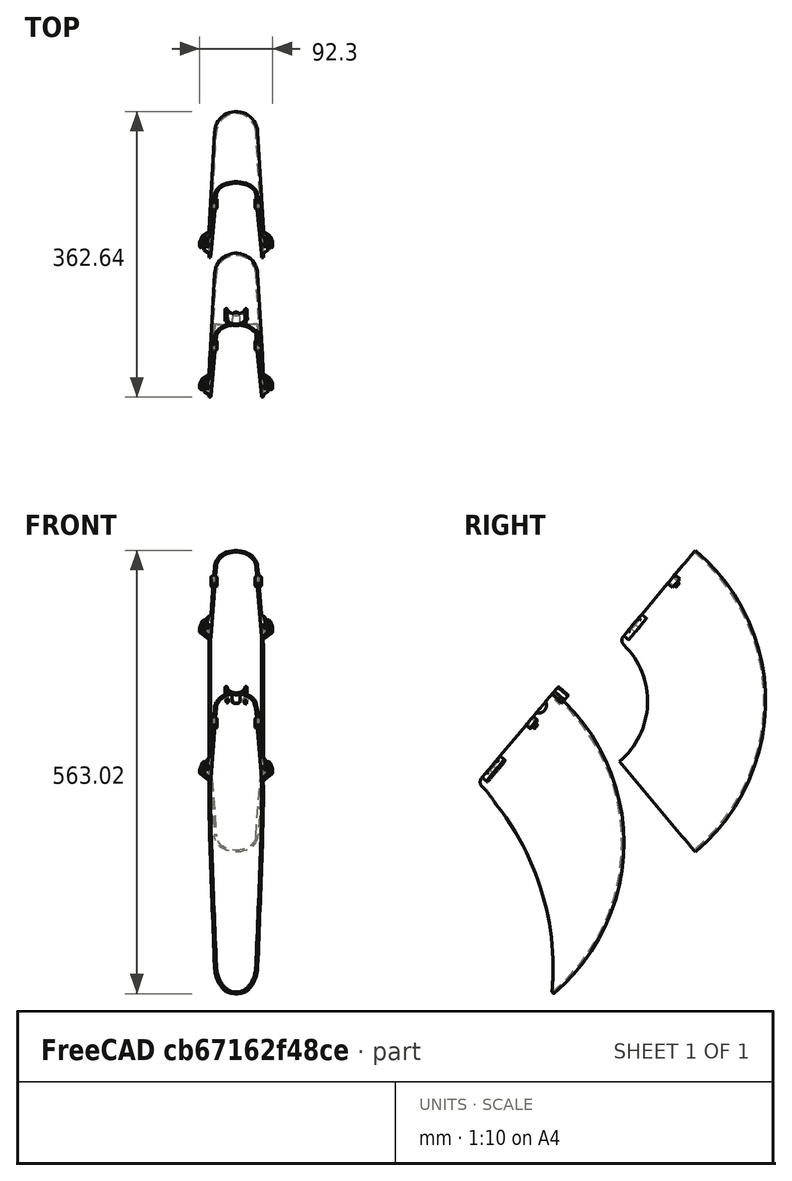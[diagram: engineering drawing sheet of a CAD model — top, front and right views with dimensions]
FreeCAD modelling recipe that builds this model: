
FCSTD DOCUMENT  (FreeCAD 0.19R)
Label: Mudguard5.1
License: All rights reserved
LicenseURL: http://en.wikipedia.org/wiki/All_rights_reserved
objects: Sketcher::SketchObject×6, Part::Cylinder×4, Part::Fillet×4, PartDesign::Fillet×3, PartDesign::Pocket×3, Part::Box×3, Part::MultiFuse×3, Part::Chamfer×3, Part::Cut×2, PartDesign::Revolution×1, PartDesign::ShapeBinder×1, PartDesign::Pad×1, PartDesign::Chamfer×1, PartDesign::Body×1, Mesh::Feature×1
note: 45 computed .brp shape members not serialized (recipe doc carries the construction recipe); baked Part::Feature solids carry a one-line shape summary decoded from their .brp

FEATURE [Sketcher::SketchObject] Sketch
  FullyConstrained = true
  MapMode = 5
  Support = -> [XY_Plane]
  sketch-geometry (9):
    g0: LineSegment StartX=-38.02 StartY=250 StartZ=0 EndX=36.46 EndY=250 EndZ=0
    g1: ArcOfCircle CenterX=1e-16 CenterY=222.456 CenterZ=0 NormalX=0 NormalY=0 NormalZ=1 AngleXU=0 Radius=27.5438 StartAngle=0.0563879 EndAngle=3.0852
    g2: ArcOfCircle CenterX=0 CenterY=222.257 CenterZ=0 NormalX=0 NormalY=0 NormalZ=1 AngleXU=0 Radius=25.0571 StartAngle=0.0604304 EndAngle=3.08116
    g3: LineSegment StartX=-34.5 StartY=100 StartZ=0 EndX=-27.5 EndY=224.009 EndZ=0
    g4: LineSegment StartX=-32.5 StartY=100 StartZ=0 EndX=-25.0114 EndY=223.77 EndZ=0
    g5: LineSegment StartX=25.0114 StartY=223.77 StartZ=0 EndX=32.5 EndY=100 EndZ=0
    g6: LineSegment StartX=-34.5 StartY=100 StartZ=0 EndX=-32.5 EndY=100 EndZ=0
    g7: LineSegment StartX=32.5 StartY=100 StartZ=0 EndX=34.5 EndY=100 EndZ=0
    g8: LineSegment StartX=34.5 StartY=100 StartZ=0 EndX=27.5 EndY=224.009 EndZ=0
  constraints (24):
    c: Horizontal(g0)
    c: DistanceY(g0) = 250
    c: Tangent(g1,g0)
    c: Symmetric(g1,g1,g-2)
    c: Distance(g0) = 74.48
    c: DistanceX(g0) = 36.46
    c: Tangent(g3,g1) = 1.5708
    c: Coincident(g6,g3)
    c: Coincident(g6,g4)
    c: Distance(g6) = 2
    c: Tangent(g4,g2) = 1.5708
    c: Tangent(g5,g2) = 1.5708
    c: PointOnObject(g2,g-2)
    c: Coincident(g5,g7)
    c: Coincident(g7,g8)
    c: Coincident(g8,g1)
    c: Symmetric(g5,g4,g-2)
    c: Symmetric(g7,g3,g-2)
    c: Horizontal(g7)
    c: Distance(g5,g4) = 65
    c: DistanceY(g7) = 100
    c: Distance(g1,g1) = 55
    c: Distance(g2,g1) = 2.5
    c: DistanceY(g2) = 223.77
FEATURE [PartDesign::Revolution] Revolution
  Angle = 100
  Axis = (1,0,0)
  Base = (0,0,0)
  Midplane = true
  Profile = -> Sketch
  ReferenceAxis = -> Sketch [H_Axis]
FEATURE [PartDesign::ShapeBinder] CopyFusion
  Placement = pos=(0,0,0) rot=(1,0,0;0.785398rad)
  TraceSupport = false
FEATURE [PartDesign::Fillet] Fillet
  Base = -> Revolution [Edge7,Edge19]
  BaseFeature = -> Revolution
  Radius = 8
  SupportTransform = false
FEATURE [Sketcher::SketchObject] Sketch002
  FullyConstrained = false
  MapMode = 5
  Placement = pos=(0,0,0) rot=(1,0,0;0.872665rad)
  Support = -> [Fillet]
  sketch-geometry (21):
    g0: LineSegment StartX=-29.785 StartY=256.106 StartZ=0 EndX=29.785 EndY=256.106 EndZ=0
    g1: LineSegment StartX=-43.3942 StartY=132.698 StartZ=0 EndX=-46.5 EndY=121.106 EndZ=0
    g2: LineSegment StartX=-46.5 StartY=121.106 StartZ=0 EndX=-33.2488 EndY=107.855 EndZ=0
    g3: LineSegment StartX=-33.2488 StartY=107.855 StartZ=0 EndX=-31 EndY=145.092 EndZ=0
    g4: LineSegment StartX=-31 StartY=145.092 StartZ=0 EndX=-43.3942 EndY=132.698 EndZ=0
    g5: LineSegment StartX=43.3942 StartY=132.698 StartZ=0 EndX=46.5 EndY=121.106 EndZ=0
    g6: LineSegment StartX=46.5 StartY=121.106 StartZ=0 EndX=33.2488 EndY=107.855 EndZ=0
    g7: LineSegment StartX=33.2488 StartY=107.855 StartZ=0 EndX=31 EndY=145.092 EndZ=0
    g8: LineSegment StartX=31 StartY=145.092 StartZ=0 EndX=43.3942 EndY=132.698 EndZ=0
    g9: LineSegment StartX=28 StartY=194.106 StartZ=0 EndX=32 EndY=198.106 EndZ=0
    g10: LineSegment StartX=32 StartY=198.106 StartZ=0 EndX=32 EndY=206.106 EndZ=0
    g11: LineSegment StartX=32 StartY=206.106 StartZ=0 EndX=28 EndY=210.106 EndZ=0
    g12: LineSegment StartX=28 StartY=210.106 StartZ=0 EndX=24 EndY=206.106 EndZ=0
    g13: LineSegment StartX=24 StartY=206.106 StartZ=0 EndX=24 EndY=198.106 EndZ=0
    g14: LineSegment StartX=24 StartY=198.106 StartZ=0 EndX=28 EndY=194.106 EndZ=0
    g15: LineSegment StartX=-28 StartY=194.106 StartZ=0 EndX=-24 EndY=198.106 EndZ=0
    g16: LineSegment StartX=-24 StartY=198.106 StartZ=0 EndX=-24 EndY=206.106 EndZ=0
    g17: LineSegment StartX=-24 StartY=206.106 StartZ=0 EndX=-28 EndY=210.106 EndZ=0
    g18: LineSegment StartX=-28 StartY=210.106 StartZ=0 EndX=-32 EndY=206.106 EndZ=0
    g19: LineSegment StartX=-32 StartY=206.106 StartZ=0 EndX=-32 EndY=198.106 EndZ=0
    g20: LineSegment StartX=-32 StartY=198.106 StartZ=0 EndX=-28 EndY=194.106 EndZ=0
  constraints (55):
    c: Coincident(g1,g2)
    c: Coincident(g2,g3)
    c: Coincident(g3,g4)
    c: Coincident(g4,g1)
    c: Coincident(g5,g6)
    c: Coincident(g6,g7)
    c: Coincident(g7,g8)
    c: Coincident(g8,g5)
    c: Symmetric(g7,g3,g-2)
    c: Symmetric(g6,g2,g-2)
    c: Equal(g5,g1)
    c: Symmetric(g5,g1,g-2)
    c: Equal(g2,g6)
    c: Distance(g5,g1) = 93
    c: Angle(g6) = -2.35619
    c: Coincident(g9,g10)
    c: Vertical(g10)
    c: Coincident(g10,g11)
    c: Coincident(g11,g12)
    c: Coincident(g12,g13)
    c: Vertical(g13)
    c: Coincident(g13,g14)
    c: Coincident(g14,g9)
    c: Coincident(g15,g16)
    c: Coincident(g16,g17)
    c: Coincident(g17,g18)
    c: Coincident(g18,g19)
    c: Coincident(g19,g20)
    c: Coincident(g20,g15)
    c: Distance(g5) = 12
    c: Angle(g5) = -1.309
    c: Symmetric(g0,g0,g-2)
    c: Distance(g0) = 59.57
    c: Angle(g8) = -0.785398
    c: Distance(g7,g3) = 62
    c: Distance(g9,g13) = 8
    c: Symmetric(g13,g15,g-2)
    c: Symmetric(g12,g16,g-2)
    c: Symmetric(g9,g19,g-2)
    c: Symmetric(g10,g18,g-2)
    c: Equal(g13,g19)
    c: Distance(g10) = 8
    c: Angle(g12,g11) = 1.5708
    c: Equal(g18,g12)
    c: Equal(g20,g14)
    c: Equal(g15,g9)
    c: Equal(g17,g11)
    c: Angle(g15,g20) = 1.5708
    c: Equal(g20,g15)
    c: Distance(g10,g0) = 50
    c: DistanceY(g12,g10) = 0
    c: Distance(g9,g19) = 64
    c: Distance(g5,g0) = 135
    c: Distance(g2) = 18.74
    c: Equal(g17,g18)
FEATURE [Sketcher::SketchObject] Sketch004
  FullyConstrained = false
  MapMode = 5
  Placement = pos=(-31,0,0) rot=(0.57735,-0.57735,-0.57735;2.0944rad)
  sketch-geometry (8):
    g0: LineSegment StartX=-122.627 StartY=164.31 StartZ=0 EndX=-119.228 EndY=159.366 EndZ=0
    g1: LineSegment StartX=-119.228 StartY=159.366 StartZ=0 EndX=-116.756 EndY=161.065 EndZ=0
    g2: LineSegment StartX=-116.756 StartY=161.065 StartZ=0 EndX=-120.154 EndY=166.009 EndZ=0
    g3: LineSegment StartX=-120.154 StartY=166.009 StartZ=0 EndX=-122.627 EndY=164.31 EndZ=0
    g4: LineSegment StartX=-76.9755 StartY=93.1865 StartZ=0 EndX=-79.4599 EndY=91.5049 EndZ=0
    g5: LineSegment StartX=-79.4599 StartY=91.5049 StartZ=0 EndX=-82.8231 EndY=96.4737 EndZ=0
    g6: LineSegment StartX=-82.8231 StartY=96.4737 StartZ=0 EndX=-80.3387 EndY=98.1553 EndZ=0
    g7: LineSegment StartX=-80.3387 StartY=98.1553 StartZ=0 EndX=-76.9755 EndY=93.1865 EndZ=0
  constraints (18):
    c: Coincident(g0,g1)
    c: Coincident(g1,g2)
    c: Coincident(g2,g3)
    c: Coincident(g3,g0)
    c: Coincident(g4,g5)
    c: Coincident(g5,g6)
    c: Coincident(g6,g7)
    c: Coincident(g7,g4)
    c: Equal(g1,g3)
    c: Equal(g3,g6)
    c: Equal(g6,g4)
    c: Distance(g6) = 3
    c: Perpendicular(g0,g3)
    c: Equal(g2,g0)
    c: Equal(g0,g5)
    c: Equal(g5,g7)
    c: Distance(g0) = 6
    c: Perpendicular(g5,g4)
FEATURE [Part::Cylinder] Cylinder001
  Angle = 360
  AttacherType = Attacher::AttachEngine3D
  Height = 250
  Placement = pos=(-100,-174,-159) rot=(0,1,0;1.5708rad)
  Radius = 334
FEATURE [Part::Cylinder] Cylinder
  Angle = 360
  AttacherType = Attacher::AttachEngine3D
  Height = 20
  Placement = pos=(35,142,175) rot=(0,-0.999201,0.039968;1.5708rad)
  Radius = 10
FEATURE [PartDesign::Pad] Pad
  BaseFeature = -> Fillet
  Direction = (1,1,1)
  Length = 8
  Length2 = 100
  Profile = -> Sketch002
  Reversed = true
  Type = 0
FEATURE [Sketcher::SketchObject] Sketch003
  FullyConstrained = true
  MapMode = 5
  Placement = pos=(0,-4.35e-14,3.65e-14) rot=(1,0,0;0.872665rad)
  Support = -> [Pad]
  sketch-geometry (8):
    g0: LineSegment StartX=35 StartY=146.87 StartZ=0 EndX=45 EndY=97.88 EndZ=0
    g1: LineSegment StartX=45 StartY=97.88 StartZ=0 EndX=47.9394 EndY=98.48 EndZ=0
    g2: LineSegment StartX=47.9394 StartY=98.48 StartZ=0 EndX=37.9394 EndY=147.47 EndZ=0
    g3: LineSegment StartX=37.9394 StartY=147.47 StartZ=0 EndX=35 EndY=146.87 EndZ=0
    g4: LineSegment StartX=-47.9394 StartY=98.48 StartZ=0 EndX=-45 EndY=97.88 EndZ=0
    g5: LineSegment StartX=-45 StartY=97.88 StartZ=0 EndX=-35 EndY=146.87 EndZ=0
    g6: LineSegment StartX=-47.9394 StartY=98.48 StartZ=0 EndX=-37.9394 EndY=147.47 EndZ=0
    g7: LineSegment StartX=-37.9394 StartY=147.47 StartZ=0 EndX=-35 EndY=146.87 EndZ=0
  constraints (22):
    c: Coincident(g0,g1)
    c: Coincident(g1,g2)
    c: Coincident(g2,g3)
    c: Coincident(g3,g0)
    c: Coincident(g4,g5)
    c: Equal(g1,g3)
    c: Equal(g0,g2)
    c: Symmetric(g4,g0,g-2)
    c: Perpendicular(g0,g1)
    c: Distance(g3) = 3
    c: Distance(g0,g4) = 90
    c: Coincident(g4,g6)
    c: Coincident(g6,g7)
    c: Coincident(g7,g5)
    c: Equal(g7,g3)
    c: Equal(g6,g5)
    c: Perpendicular(g6,g7)
    c: Symmetric(g0,g5,g-2)
    c: Distance(g2) = 50
    c: Equal(g4,g7)
    c: DistanceY(g0) = 97.88
    c: Distance(g5,g0) = 70
FEATURE [PartDesign::Pocket] Pocket
  BaseFeature = -> Pad
  Length = 2
  Length2 = 100
  Profile = -> Sketch003
  Type = 0
FEATURE [PartDesign::Chamfer] Chamfer
  Angle = 45
  Base = -> Pocket [Edge139,Edge101,Edge142,Edge145]
  BaseFeature = -> Pocket
  ChamferType = 0
  FlipDirection = false
  Size = 1
  Size2 = 1
  SupportTransform = false
FEATURE [Sketcher::SketchObject] Sketch005
  FullyConstrained = false
  MapMode = 5
  Placement = pos=(-3.5e-15,6.12836,-5.1423) rot=(0,0.906308,0.422618;3.14159rad)
  Support = -> [Chamfer]
  sketch-geometry (8):
    g0: LineSegment StartX=-37.5477 StartY=128.579 StartZ=0 EndX=-34.5477 EndY=128.579 EndZ=0
    g1: LineSegment StartX=-34.5477 StartY=128.579 StartZ=0 EndX=-34.5477 EndY=121.579 EndZ=0
    g2: LineSegment StartX=-34.5477 StartY=121.579 StartZ=0 EndX=-37.5477 EndY=121.579 EndZ=0
    g3: LineSegment StartX=-37.5477 StartY=121.579 StartZ=0 EndX=-37.5477 EndY=128.579 EndZ=0
    g4: LineSegment StartX=34.5477 StartY=128.579 StartZ=0 EndX=37.5477 EndY=128.579 EndZ=0
    g5: LineSegment StartX=37.5477 StartY=128.579 StartZ=0 EndX=37.5477 EndY=121.579 EndZ=0
    g6: LineSegment StartX=37.5477 StartY=121.579 StartZ=0 EndX=34.5477 EndY=121.579 EndZ=0
    g7: LineSegment StartX=34.5477 StartY=121.579 StartZ=0 EndX=34.5477 EndY=128.579 EndZ=0
  constraints (21):
    c: Coincident(g0,g1)
    c: Coincident(g1,g2)
    c: Coincident(g2,g3)
    c: Coincident(g3,g0)
    c: Horizontal(g0)
    c: Horizontal(g2)
    c: Vertical(g1)
    c: Vertical(g3)
    c: Coincident(g4,g5)
    c: Coincident(g5,g6)
    c: Coincident(g6,g7)
    c: Coincident(g7,g4)
    c: Horizontal(g4)
    c: Horizontal(g6)
    c: Vertical(g5)
    c: Vertical(g7)
    c: Distance(g4) = 3
    c: Distance(g5) = 7
    c: Equal(g4,g0)
    c: Symmetric(g0,g4,g-2)
    c: Equal(g1,g5)
FEATURE [PartDesign::Pocket] Pocket001
  BaseFeature = -> Chamfer
  Length = 5
  Length2 = 100
  Profile = -> Sketch005
  Type = 1
FEATURE [Sketcher::SketchObject] Sketch006
  FullyConstrained = false
  MapMode = 5
  Placement = pos=(-32,0,0) rot=(0.57735,-0.57735,-0.57735;2.0944rad)
  Support = -> [Pocket001]
  sketch-geometry (4):
    g0: LineSegment StartX=-140.408 StartY=149.728 StartZ=0 EndX=-136.658 EndY=145.045 EndZ=0
    g1: LineSegment StartX=-136.658 StartY=145.045 StartZ=0 EndX=-134.316 EndY=146.92 EndZ=0
    g2: LineSegment StartX=-134.316 StartY=146.92 StartZ=0 EndX=-138.067 EndY=151.603 EndZ=0
    g3: LineSegment StartX=-138.067 StartY=151.603 StartZ=0 EndX=-140.408 EndY=149.728 EndZ=0
  constraints (9):
    c: Coincident(g0,g1)
    c: Coincident(g1,g2)
    c: Coincident(g2,g3)
    c: Coincident(g3,g0)
    c: Equal(g1,g3)
    c: Perpendicular(g1,g0)
    c: Equal(g2,g0)
    c: Distance(g2) = 6
    c: Distance(g3) = 3
FEATURE [PartDesign::Pocket] Pocket002
  BaseFeature = -> Pocket001
  Length = 5
  Length2 = 100
  Profile = -> Sketch006
  Type = 1
FEATURE [PartDesign::Fillet] Fillet001
  Base = -> Pocket002 [Edge46,Edge7,Edge169,Edge149]
  BaseFeature = -> Pocket002
  Radius = 3
  SupportTransform = false
FEATURE [PartDesign::Fillet] Fillet002
  Base = -> Fillet001 [Edge92,Edge96,Edge184,Edge171]
  BaseFeature = -> Fillet001
  Radius = 1
  SupportTransform = false
FEATURE [PartDesign::Body] Body
  Group = -> [Sketch,Revolution,CopyFusion,Fillet,Sketch002,Sketch003,Sketch004,Pad,Pocket,Chamfer,Sketch005,Pocket001,Sketch006,Pocket002,Fillet001,Fillet002]
  Origin = -> Origin
  Tip = -> Fillet002
FEATURE [Part::Cylinder] Cylinder002
  Angle = 360
  AttacherType = Attacher::AttachEngine3D
  Height = 17
  Placement = pos=(0,180,188) rot=(1,0,0;0.872665rad)
  Radius = 14
FEATURE [Part::Cylinder] Cylinder003
  Angle = 360
  AttacherType = Attacher::AttachEngine3D
  Height = 47
  Placement = pos=(0,182,187) rot=(1,0,0;0.872665rad)
  Radius = 11.5
FEATURE [Part::Box] Box  label="Cube"
  AttacherType = Attacher::AttachEngine3D
  Height = 50
  Length = 50
  Placement = pos=(-17,165,200) rot=(1,0,0;-0.715585rad)
  Width = 50
FEATURE [Part::MultiFuse] Fusion001
  Shapes = -> [Cylinder002,Fillet002]
FEATURE [Part::MultiFuse] Fusion
  Shapes = -> [Cylinder,Cylinder001,Cylinder003,Box]
FEATURE [Part::Cut] Cut
  Base = -> Fusion001
  Tool = -> Fusion
FEATURE [Part::Fillet] Fillet003
  Base = -> Cut
  Edges = 2 edges r=3: [Edge3,Edge17]
FEATURE [Part::Chamfer] Chamfer001
  Base = -> Fillet003
  Edges = 2 edges r=1: [Edge55,Edge83]
FEATURE [Part::Chamfer] Chamfer002
  Base = -> Chamfer001
  Edges = 2 edges r=1: [Edge103,Edge271]
FEATURE [Part::Fillet] Fillet004
  Base = -> Chamfer002
  Edges = 2 edges r=1.9: [Edge69,Edge310]
FEATURE [Part::Chamfer] Chamfer003
  Base = -> Fillet004
  Edges = 2 edges r=1.7: [Edge99,Edge272]
FEATURE [Part::Fillet] Fillet005
  Base = -> Chamfer003
  Edges = 2 edges r=1: [Edge253,Edge254]
  Placement = pos=(0,-180,-180) rot=(1,0,0;0rad)
FEATURE [Part::Fillet] Fillet006
  Base = -> Fillet005
  Edges = 2 edges r=0.5: [Edge16,Edge40]
FEATURE [Part::Box] Box001  label="Cube001"
  AttacherType = Attacher::AttachEngine3D
  Height = 20
  Length = 6
  Placement = pos=(12,-18,-2) rot=(-0.096674,0.483368,0.870063;1.5708rad)
  Width = 3
FEATURE [Part::Box] Box002  label="Cube002"
  AttacherType = Attacher::AttachEngine3D
  Height = 20
  Length = 6
  Placement = pos=(-12,-13,-3) rot=(0,0.518978,0.854788;-1.48353rad)
  Width = 3
FEATURE [Part::MultiFuse] Fusion002
  Shapes = -> [Box002,Box001]
FEATURE [Part::Cut] Cut001
  Base = -> Fillet006
  Tool = -> Fusion002
FEATURE [Mesh::Feature] Mesh  label="Cut001 (Meshed)"
